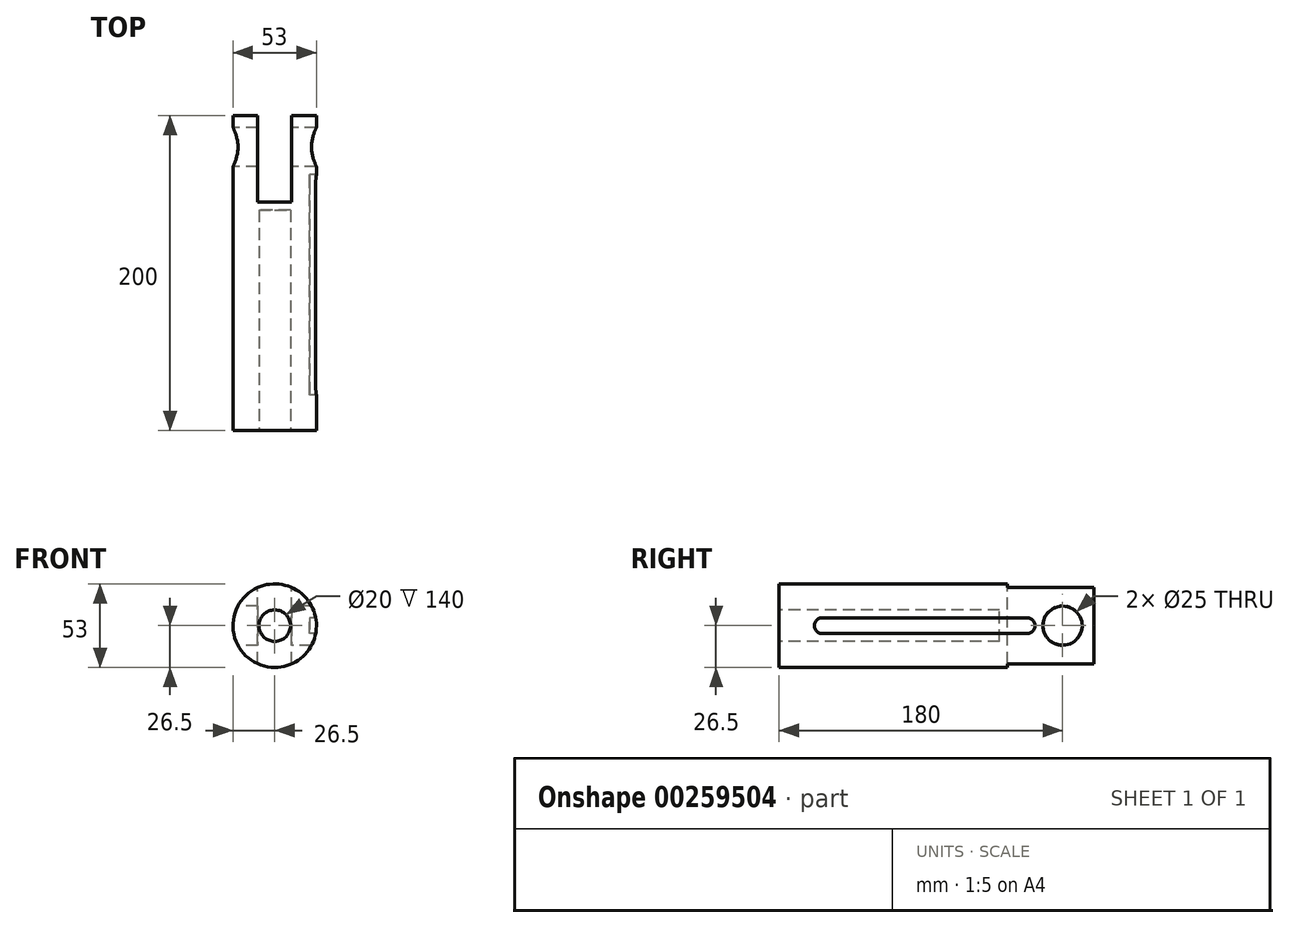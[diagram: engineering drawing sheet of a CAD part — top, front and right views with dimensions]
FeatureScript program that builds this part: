
annotation { "Feature Type Name" : "Feature", "Feature Type Description" : "" }
export const myFeature = defineFeature(function(context is Context, id is Id, definition is map)
    precondition{}
    {
        {
            var Q0;
            Q0=qCreatedBy(makeId("Front.planeOp"),FACE);
            var sketch = newSketch(context, id + "F0", { "sketchPlane" : qUnion([Q0])});
            skCircle(sketch, "E0", {"center": v(0, 0) * mm, "radius": 26.5 * mm});
            skSolve(sketch);
        }
        {
            var Q0;
            Q0 = qSketchRegion(id + "F0", true);
            extrude(context, id + "F1", {"entities" : qUnion([Q0]), "depth" : 200 * mm});
        }
        {
            var Q0;
            Q0=qCreatedBy(makeId("Right.planeOp"),FACE);
            var sketch = newSketch(context, id + "F2", { "sketchPlane" : qUnion([Q0])});
            skCircle(sketch, "E1", {"center": v(-20, 0) * mm, "radius": 12.5 * mm});
            skSolve(sketch);
        }
        {
            var Q0;
            Q0 = qSketchRegion(id + "F2", true);
            extrude(context, id + "F3", {"entities" : qUnion([Q0]), "operationType" : NewBodyOperationType.REMOVE, "depth" : 60 * mm, "symmetric" : true});
        }
        {
            var Q0;
            Q0=qCreatedBy(makeId("Front.planeOp"),FACE);
            var sketch = newSketch(context, id + "F4", { "sketchPlane" : qUnion([Q0])});
            skLineSegment(sketch, "E2.bottom", {"start": v(10.75, -30) * mm, "end": v(-10.75, -30) * mm});
            skLineSegment(sketch, "E2.top", {"start": v(10.75, 30) * mm, "end": v(-10.75, 30) * mm});
            skLineSegment(sketch, "E2.left", {"start": v(10.75, -30) * mm, "end": v(10.75, 30) * mm});
            skLineSegment(sketch, "E2.right", {"start": v(-10.75, -30) * mm, "end": v(-10.75, 30) * mm});
            skSolve(sketch);
        }
        {
            var Q0;
            Q0 = qSketchRegion(id + "F4", true);
            extrude(context, id + "F5", {"entities" : qUnion([Q0]), "operationType" : NewBodyOperationType.REMOVE, "depth" : 55 * mm});
        }
        {
            var Q0;
            Q0=qCreatedBy(makeId("Right.planeOp"),FACE);
            cPlane(context, id + "F6", {"entities" : qUnion([Q0]), "cplaneType" : CPlaneType.OFFSET, "offset" : 22 * mm, "width" : 150 * mm, "height" : 150 * mm});
        }
        {
            var Q0;
            Q0=qCreatedBy(id+"F6.planeOp",FACE);
            var sketch = newSketch(context, id + "F7", { "sketchPlane" : qUnion([Q0])});
            skLineSegment(sketch, "E3", {"start": v(-172.63, 4.99) * mm, "end": v(-42.63, 5) * mm});
            skLineSegment(sketch, "E4", {"start": v(-42.63, -5) * mm, "end": v(-172.63, -5.01) * mm});
            skArc(sketch, "E5", {"start": v(-42.63, 5) * mm, "mid": v(-37.63, 0) * mm, "end": v(-42.63, -5) * mm});
            skArc(sketch, "E6", {"start": v(-172.63, 4.99) * mm, "mid": v(-177.63, -0.01) * mm, "end": v(-172.63, -5.01) * mm});
            skSolve(sketch);
        }
        {
            var Q0;
            Q0 = qSketchRegion(id + "F7", true);
            extrude(context, id + "F8", {"entities" : qUnion([Q0]), "operationType" : NewBodyOperationType.REMOVE, "depth" : 10 * mm});
        }
        {
            var Q0;
            Q0=makeQuery(id+"F1.opExtrude","CAP_FACE",FACE,{"disambiguationData":[OSD([sQuery(id+"F0.wireOp",EDGE,"E0")])],"isStart":false});
            var sketch = newSketch(context, id + "F9", { "sketchPlane" : qUnion([Q0])});
            skCircle(sketch, "E7", {"center": v(0, 0) * mm, "radius": 10 * mm});
            skSolve(sketch);
        }
        {
            var Q0;
            Q0 = qSketchRegion(id + "F9", true);
            extrude(context, id + "F10", {"entities" : qUnion([Q0]), "operationType" : NewBodyOperationType.REMOVE, "oppositeDirection" : true, "depth" : 140 * mm});
        }
    });
